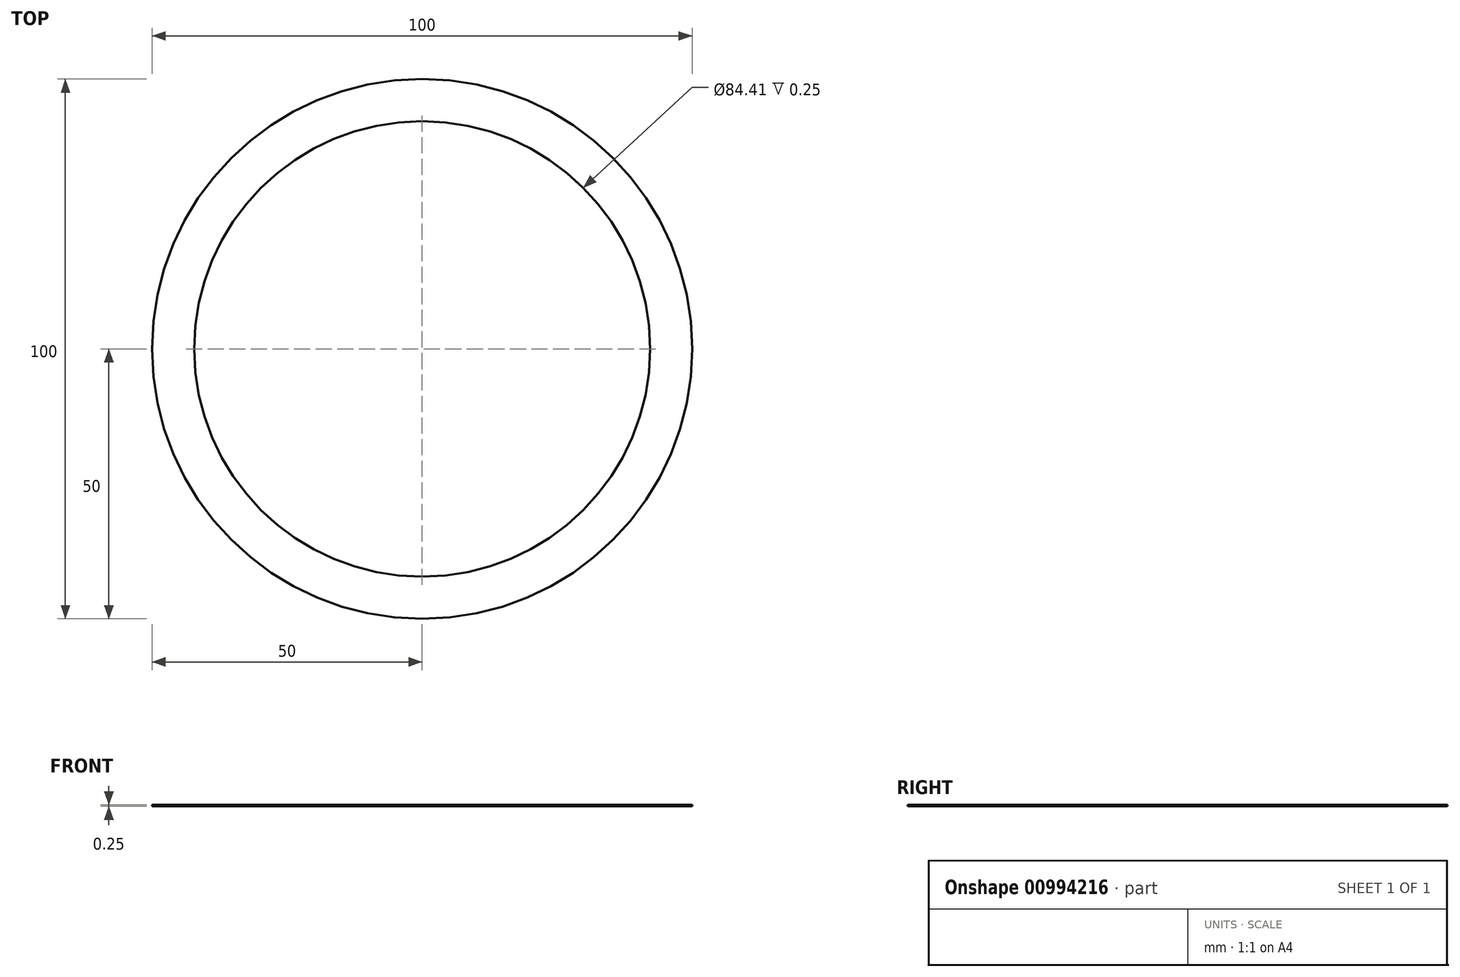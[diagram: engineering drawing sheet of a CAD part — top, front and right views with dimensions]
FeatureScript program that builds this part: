
annotation { "Feature Type Name" : "Feature", "Feature Type Description" : "" }
export const myFeature = defineFeature(function(context is Context, id is Id, definition is map)
    precondition{}
    {
        {
            var Q0;
            Q0=qCreatedBy(makeId("Top.planeOp"),FACE);
            var sketch = newSketch(context, id + "F0", { "sketchPlane" : qUnion([Q0])});
            skCircle(sketch, "E0", {"center": v(0, 0) * mm, "radius": 50 * mm});
            skSolve(sketch);
        }
        {
            var Q0;
            Q0 = qSketchRegion(id + "F0", true);
            extrude(context, id + "F1", {"entities" : qUnion([Q0]), "depth" : .25 * mm, "offsetDistance" : 25 * mm});
        }
        {
            var Q0;
            Q0=makeQuery(id+"F1.opExtrude","CAP_FACE",FACE,{"disambiguationData":[OSD([sQuery(id+"F0.wireOp",EDGE,"E0")])],"isStart":false});
            var sketch = newSketch(context, id + "F2", { "sketchPlane" : qUnion([Q0])});
            skCircle(sketch, "E1", {"center": v(0, 0) * mm, "radius": 42.2 * mm});
            skSolve(sketch);
        }
        {
            var Q0;
            Q0 = qSketchRegion(id + "F2", true);
            extrude(context, id + "F3", {"entities" : qUnion([Q0]), "operationType" : NewBodyOperationType.REMOVE, "oppositeDirection" : true, "depth" : 25 * mm, "offsetDistance" : 25 * mm});
        }
    });
